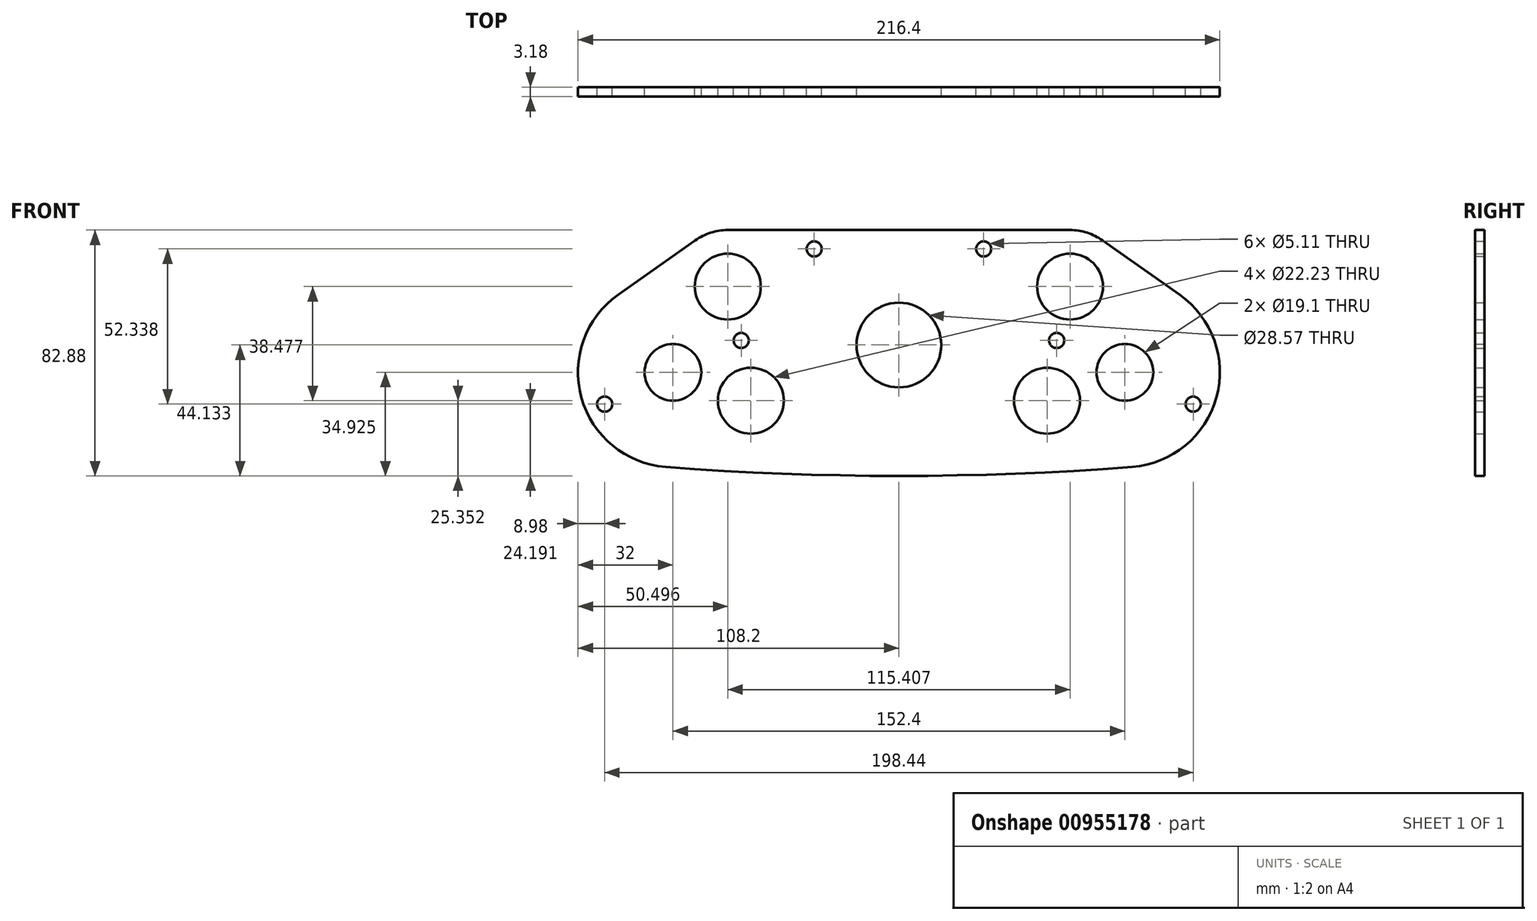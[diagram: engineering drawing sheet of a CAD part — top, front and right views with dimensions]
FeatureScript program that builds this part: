
annotation { "Feature Type Name" : "Feature", "Feature Type Description" : "" }
export const myFeature = defineFeature(function(context is Context, id is Id, definition is map)
    precondition{}
    {
        {
            var Q0;
            Q0=qCreatedBy(makeId("Front.planeOp"),FACE);
            var sketch = newSketch(context, id + "F0", { "sketchPlane" : qUnion([Q0])});
            skCircle(sketch, "E0", {"center": v(-76.2, 60.32) * mm, "radius": 32 * mm, "construction": true});
            skCircle(sketch, "E1", {"center": v(76.2, 60.33) * mm, "radius": 32 * mm, "construction": true});
            skLineSegment(sketch, "E2", {"start": v(-76.2, 60.32) * mm, "end": v(76.2, 60.32) * mm, "construction": true});
            skLineSegment(sketch, "E3", {"start": v(0, 60.32) * mm, "end": v(0, 0) * mm, "construction": true});
            skCircle(sketch, "E4", {"center": v(-76.2, 60.32) * mm, "radius": 7.63 * mm, "construction": true});
            skCircle(sketch, "E5", {"center": v(76.2, 60.33) * mm, "radius": 7.63 * mm, "construction": true});
            skLineSegment(sketch, "E6.bottom", {"start": v(-127, 25.4) * mm, "end": v(127, 25.4) * mm, "construction": true});
            skLineSegment(sketch, "E6.top", {"start": v(-127, -25.4) * mm, "end": v(127, -25.4) * mm, "construction": true});
            skLineSegment(sketch, "E6.left", {"start": v(-127, 25.4) * mm, "end": v(-127, -25.4) * mm, "construction": true});
            skLineSegment(sketch, "E6.right", {"start": v(127, 25.4) * mm, "end": v(127, -25.4) * mm, "construction": true});
            skPoint(sketch, "E6.middle", {"position": v(0, -1.59) * mm});
            skCircle(sketch, "E7", {"center": v(0, -1.59) * mm, "radius": 50.8 * mm, "construction": true});
            skCircle(sketch, "E8", {"center": v(-57.7, 89.23) * mm, "radius": 26.68 * mm, "construction": true});
            skCircle(sketch, "E9", {"center": v(57.7, 89.23) * mm, "radius": 26.68 * mm, "construction": true});
            skCircle(sketch, "E10", {"center": v(0, 69.53) * mm, "radius": 34.3 * mm, "construction": true});
            skCircle(sketch, "E11", {"center": v(0, 69.53) * mm, "radius": 25.4 * mm, "construction": true});
            skCircle(sketch, "E12", {"center": v(0, 69.53) * mm, "radius": 38.1 * mm, "construction": true});
            skCircle(sketch, "E13", {"center": v(0, -1.59) * mm, "radius": 33.02 * mm, "construction": true});
            skCircle(sketch, "E14", {"center": v(0, -1.59) * mm, "radius": 45.72 * mm, "construction": true});
            skCircle(sketch, "E15", {"center": v(-76.2, 60.32) * mm, "radius": 9.55 * mm});
            skCircle(sketch, "E16", {"center": v(76.2, 60.33) * mm, "radius": 9.55 * mm});
            skCircle(sketch, "E17", {"center": v(-57.7, 89.23) * mm, "radius": 11.11 * mm});
            skCircle(sketch, "E18", {"center": v(57.7, 89.23) * mm, "radius": 11.11 * mm});
            skCircle(sketch, "E19", {"center": v(0, 69.53) * mm, "radius": 14.29 * mm});
            skCircle(sketch, "E20", {"center": v(0, -1.59) * mm, "radius": 14.29 * mm});
            skPoint(sketch, "E21.middle", {"position": v(0, 0) * mm});
            skCircle(sketch, "E22", {"center": v(-38.1, 12.7) * mm, "radius": 9.53 * mm, "construction": true});
            skCircle(sketch, "E23", {"center": v(-38.1, -12.7) * mm, "radius": 9.53 * mm, "construction": true});
            skCircle(sketch, "E24", {"center": v(38.1, -12.7) * mm, "radius": 9.53 * mm, "construction": true});
            skCircle(sketch, "E25", {"center": v(38.1, 12.7) * mm, "radius": 9.53 * mm, "construction": true});
            skCircle(sketch, "E26", {"center": v(38.1, 0) * mm, "radius": 9.53 * mm, "construction": true});
            skCircle(sketch, "E27", {"center": v(-38.1, 0) * mm, "radius": 9.53 * mm, "construction": true});
            skCircle(sketch, "E28", {"center": v(38.1, -12.7) * mm, "radius": 2.55 * mm});
            skCircle(sketch, "E29", {"center": v(38.1, 0) * mm, "radius": 2.55 * mm, "construction": true});
            skCircle(sketch, "E30", {"center": v(38.1, 12.7) * mm, "radius": 2.55 * mm});
            skCircle(sketch, "E31", {"center": v(-38.1, 12.7) * mm, "radius": 2.55 * mm});
            skCircle(sketch, "E32", {"center": v(-38.1, 0) * mm, "radius": 2.55 * mm, "construction": true});
            skCircle(sketch, "E33", {"center": v(-38.1, -12.7) * mm, "radius": 2.55 * mm});
            skLineSegment(sketch, "E34", {"start": v(-45.02, -19.24) * mm, "end": v(-99.46, 38.34) * mm});
            skArc(sketch, "E35", {"start": v(-45.02, -19.24) * mm, "mid": v(-42.05, -21.37) * mm, "end": v(-38.5, -22.22) * mm});
            skArc(sketch, "E36", {"start": v(38.5, -22.22) * mm, "mid": v(42.05, -21.37) * mm, "end": v(45.02, -19.24) * mm});
            skLineSegment(sketch, "E37", {"start": v(45.02, -19.24) * mm, "end": v(99.46, 38.34) * mm});
            skCircle(sketch, "E38", {"center": v(57.7, 89.23) * mm, "radius": 19.05 * mm, "construction": true});
            skCircle(sketch, "E39", {"center": v(-57.7, 89.23) * mm, "radius": 19.05 * mm, "construction": true});
            skArc(sketch, "E40", {"start": v(99.46, 38.34) * mm, "mid": v(108.05, 63.5) * mm, "end": v(94.65, 86.48) * mm});
            skArc(sketch, "E41", {"start": v(-94.65, 86.48) * mm, "mid": v(-108.05, 63.5) * mm, "end": v(-99.46, 38.34) * mm});
            skLineSegment(sketch, "E42", {"start": v(-53.18, 71.06) * mm, "end": v(-76.2, 60.32) * mm, "construction": true});
            skLineSegment(sketch, "E43", {"start": v(-76.2, 60.32) * mm, "end": v(-99.22, 49.6) * mm, "construction": true});
            skCircle(sketch, "E44", {"center": v(-99.22, 49.6) * mm, "radius": 2.55 * mm});
            skCircle(sketch, "E45", {"center": v(-53.18, 71.06) * mm, "radius": 2.55 * mm});
            skCircle(sketch, "E46.MirrorC", {"center": v(53.18, 71.06) * mm, "radius": 2.55 * mm});
            skLineSegment(sketch, "E47.MirrorCS", {"start": v(53.18, 71.06) * mm, "end": v(76.2, 60.33) * mm, "construction": true});
            skLineSegment(sketch, "E48.MirrorCS", {"start": v(76.2, 60.33) * mm, "end": v(99.22, 49.6) * mm, "construction": true});
            skCircle(sketch, "E49.MirrorC", {"center": v(99.22, 49.6) * mm, "radius": 2.55 * mm});
            skLineSegment(sketch, "E50", {"start": v(94.65, 86.48) * mm, "end": v(68.69, 104.8) * mm});
            skLineSegment(sketch, "E51", {"start": v(-94.65, 86.48) * mm, "end": v(-68.69, 104.8) * mm});
            skLineSegment(sketch, "E52", {"start": v(-57.7, 108.28) * mm, "end": v(57.7, 108.28) * mm});
            skArc(sketch, "E53", {"start": v(-68.69, 104.8) * mm, "mid": v(-63.46, 107.39) * mm, "end": v(-57.7, 108.28) * mm});
            skArc(sketch, "E54", {"start": v(57.7, 108.28) * mm, "mid": v(63.46, 107.39) * mm, "end": v(68.69, 104.8) * mm});
            skCircle(sketch, "E55", {"center": v(0, -1.59) * mm, "radius": 22.23 * mm, "construction": true});
            skLineSegment(sketch, "E56", {"start": v(38.5, -22.22) * mm, "end": v(0.93, -23.8) * mm});
            skLineSegment(sketch, "E57", {"start": v(-38.5, -22.22) * mm, "end": v(-0.93, -23.8) * mm});
            skArc(sketch, "E58", {"start": v(-0.93, -23.8) * mm, "mid": v(0, -23.81) * mm, "end": v(0.93, -23.8) * mm});
            skLineSegment(sketch, "E59.bottom", {"start": v(-38.1, -12.7) * mm, "end": v(38.1, -12.7) * mm, "construction": true});
            skLineSegment(sketch, "E59.top", {"start": v(-38.1, 12.7) * mm, "end": v(38.1, 12.7) * mm, "construction": true});
            skLineSegment(sketch, "E59.left", {"start": v(-38.1, -12.7) * mm, "end": v(-38.1, 12.7) * mm, "construction": true});
            skLineSegment(sketch, "E59.right", {"start": v(38.1, -12.7) * mm, "end": v(38.1, 12.7) * mm, "construction": true});
            skCircle(sketch, "E60", {"center": v(-28.58, 101.93) * mm, "radius": 6.35 * mm, "construction": true});
            skCircle(sketch, "E61", {"center": v(-28.58, 101.93) * mm, "radius": 2.55 * mm});
            skCircle(sketch, "E62.MirrorC", {"center": v(28.57, 101.93) * mm, "radius": 6.35 * mm, "construction": true});
            skCircle(sketch, "E63.MirrorC", {"center": v(28.57, 101.93) * mm, "radius": 2.55 * mm});
            skCircle(sketch, "E64", {"center": v(-53.97, -1.59) * mm, "radius": 7.94 * mm, "construction": true});
            skCircle(sketch, "E65", {"center": v(-53.97, -1.59) * mm, "radius": 2.55 * mm});
            skCircle(sketch, "E66.MirrorC", {"center": v(53.98, -1.59) * mm, "radius": 7.94 * mm, "construction": true});
            skCircle(sketch, "E67.MirrorC", {"center": v(53.98, -1.59) * mm, "radius": 2.55 * mm});
            skCircle(sketch, "E68", {"center": v(-50.8, 21.9) * mm, "radius": 6.35 * mm, "construction": true});
            skCircle(sketch, "E69", {"center": v(50.8, 21.9) * mm, "radius": 6.35 * mm, "construction": true});
            skCircle(sketch, "E70", {"center": v(50.8, 21.9) * mm, "radius": 2.55 * mm});
            skCircle(sketch, "E71", {"center": v(-50.8, 21.9) * mm, "radius": 2.55 * mm});
            skLineSegment(sketch, "E72", {"start": v(50.8, 21.9) * mm, "end": v(-50.8, 21.9) * mm, "construction": true});
            skLineSegment(sketch, "E73", {"start": v(0, 21.9) * mm, "end": v(0, 69.53) * mm, "construction": true});
            skCircle(sketch, "E74", {"center": v(-76.2, 60.32) * mm, "radius": 8.9 * mm, "construction": true});
            skCircle(sketch, "E75", {"center": v(76.2, 60.33) * mm, "radius": 8.9 * mm, "construction": true});
            skCircle(sketch, "E76", {"center": v(-49.94, 50.75) * mm, "radius": 19.06 * mm, "construction": true});
            skCircle(sketch, "E77", {"center": v(-49.94, 50.75) * mm, "radius": 11.11 * mm});
            skCircle(sketch, "E78.MirrorC", {"center": v(49.94, 50.75) * mm, "radius": 11.11 * mm});
            skCircle(sketch, "E79.MirrorC", {"center": v(49.94, 50.75) * mm, "radius": 19.06 * mm, "construction": true});
            skLineSegment(sketch, "E80", {"start": v(0, 12.7) * mm, "end": v(0, -1.59) * mm, "construction": true});
            skLineSegment(sketch, "E81", {"start": v(-14.29, -1.59) * mm, "end": v(14.29, -1.59) * mm, "construction": true});
            skLineSegment(sketch, "E82", {"start": v(0, -25.4) * mm, "end": v(0, 0) * mm, "construction": true});
            skSolve(sketch);
        }
        {
            var Q0;
            Q0=qSketchRegion(id+"F0",true);
            extrude(context, id + "F1", {"entities" : qUnion([Q0]), "depth" : 3.17 * mm, "offsetDistance" : 25.4 * mm});
        }
        {
            var Q0;
            Q0=makeQuery(id+"F1.opExtrude","CAP_FACE",FACE,{"disambiguationData":[OSD([sQuery(id+"F0.wireOp",EDGE,"E15"),sQuery(id+"F0.wireOp",EDGE,"E16"),sQuery(id+"F0.wireOp",EDGE,"E17"),sQuery(id+"F0.wireOp",EDGE,"E18"),sQuery(id+"F0.wireOp",EDGE,"E19"),sQuery(id+"F0.wireOp",EDGE,"E20"),sQuery(id+"F0.wireOp",EDGE,"E28"),sQuery(id+"F0.wireOp",EDGE,"E30"),sQuery(id+"F0.wireOp",EDGE,"E31"),sQuery(id+"F0.wireOp",EDGE,"E33"),sQuery(id+"F0.wireOp",EDGE,"E34"),sQuery(id+"F0.wireOp",EDGE,"E35"),sQuery(id+"F0.wireOp",EDGE,"E36"),sQuery(id+"F0.wireOp",EDGE,"E37"),sQuery(id+"F0.wireOp",EDGE,"E40"),sQuery(id+"F0.wireOp",EDGE,"E41"),sQuery(id+"F0.wireOp",EDGE,"E44"),sQuery(id+"F0.wireOp",EDGE,"E45"),sQuery(id+"F0.wireOp",EDGE,"E46.MirrorC"),sQuery(id+"F0.wireOp",EDGE,"E49.MirrorC"),sQuery(id+"F0.wireOp",EDGE,"E50"),sQuery(id+"F0.wireOp",EDGE,"E51"),sQuery(id+"F0.wireOp",EDGE,"E52"),sQuery(id+"F0.wireOp",EDGE,"E53"),sQuery(id+"F0.wireOp",EDGE,"E54"),sQuery(id+"F0.wireOp",EDGE,"E56"),sQuery(id+"F0.wireOp",EDGE,"E57"),sQuery(id+"F0.wireOp",EDGE,"E58"),sQuery(id+"F0.wireOp",EDGE,"E61"),sQuery(id+"F0.wireOp",EDGE,"E63.MirrorC"),sQuery(id+"F0.wireOp",EDGE,"E65"),sQuery(id+"F0.wireOp",EDGE,"E67.MirrorC"),sQuery(id+"F0.wireOp",EDGE,"E70"),sQuery(id+"F0.wireOp",EDGE,"E71"),sQuery(id+"F0.wireOp",EDGE,"E77"),sQuery(id+"F0.wireOp",EDGE,"E78.MirrorC")])],"isStart":false});
            var sketch = newSketch(context, id + "F2", { "sketchPlane" : qUnion([Q0])});
            skArc(sketch, "E83", {"start": v(-99.46, 38.34) * mm, "mid": v(-89.98, 31.44) * mm, "end": v(-78.65, 28.41) * mm});
            skArc(sketch, "E84", {"start": v(-78.65, 28.41) * mm, "mid": v(0, 25.4) * mm, "end": v(78.65, 28.41) * mm});
            skArc(sketch, "E85", {"start": v(78.65, 28.41) * mm, "mid": v(89.98, 31.44) * mm, "end": v(99.46, 38.34) * mm});
            skArc(sketch, "E86", {"start": v(-99.46, 38.34) * mm, "mid": v(-108.05, 63.5) * mm, "end": v(-94.65, 86.48) * mm});
            skLineSegment(sketch, "E87", {"start": v(-94.65, 86.48) * mm, "end": v(-68.69, 104.8) * mm});
            skArc(sketch, "E88", {"start": v(-68.69, 104.8) * mm, "mid": v(-63.46, 107.39) * mm, "end": v(-57.7, 108.28) * mm});
            skLineSegment(sketch, "E89", {"start": v(-57.7, 108.28) * mm, "end": v(57.7, 108.28) * mm});
            skArc(sketch, "E90", {"start": v(57.7, 108.28) * mm, "mid": v(63.46, 107.39) * mm, "end": v(68.69, 104.8) * mm});
            skLineSegment(sketch, "E91", {"start": v(68.69, 104.8) * mm, "end": v(94.65, 86.48) * mm});
            skArc(sketch, "E92", {"start": v(94.65, 86.48) * mm, "mid": v(108.05, 63.5) * mm, "end": v(99.46, 38.34) * mm});
            skLineSegment(sketch, "E93", {"start": v(-99.46, 38.34) * mm, "end": v(-99.46, -25.4) * mm});
            skLineSegment(sketch, "E94", {"start": v(-99.46, -25.4) * mm, "end": v(99.46, -25.4) * mm});
            skLineSegment(sketch, "E95", {"start": v(99.46, -25.4) * mm, "end": v(99.46, 38.34) * mm});
            skSolve(sketch);
        }
        {
            var Q0;
            Q0=makeQuery(id+"F2.imprint","IMPRINT",FACE,{"disambiguationData":[TD([[makeQuery(id+"F2.imprint","IMPRINT",EDGE,{"derivedFrom":sQuery(id+"F2.wireOp",EDGE,"E93")}),1.0]])]});
            var Q1;
            Q1=makeQuery(id+"F2.imprint","IMPRINT",FACE,{"disambiguationData":[TD([[makeQuery(id+"F2.imprint","IMPRINT",EDGE,{"derivedFrom":sQuery(id+"F2.wireOp",EDGE,"E83")}),-1.0]])]});
            extrude(context, id + "F3", {"entities" : qUnion([Q0, Q1]), "operationType" : NewBodyOperationType.REMOVE, "oppositeDirection" : true, "depth" : 25.4 * mm, "offsetDistance" : 25.4 * mm});
        }
    });
